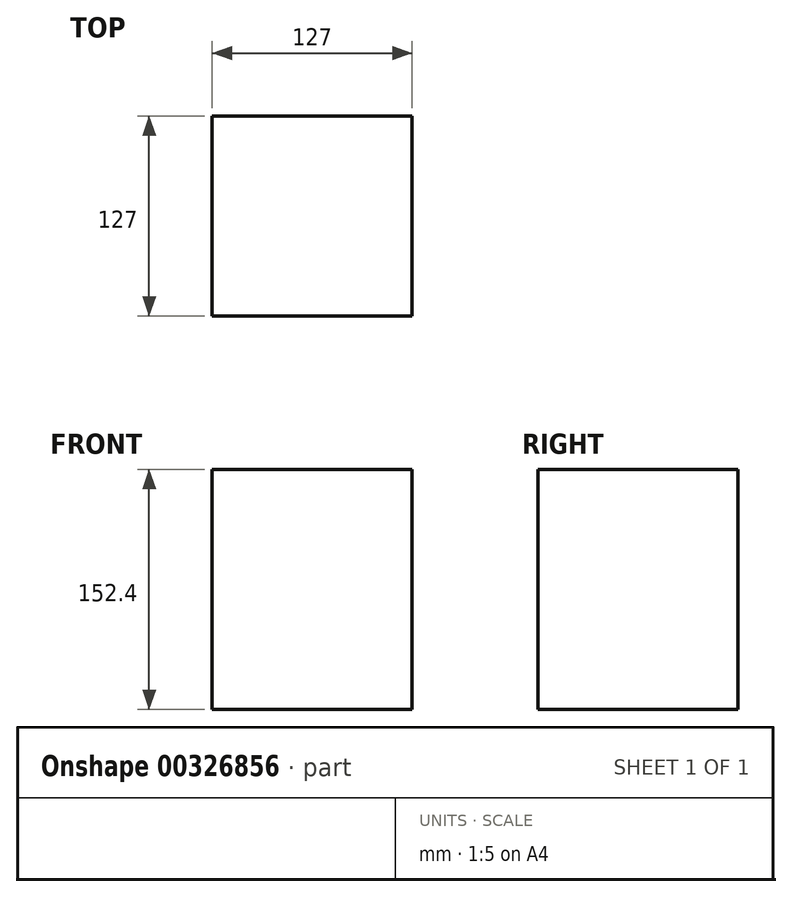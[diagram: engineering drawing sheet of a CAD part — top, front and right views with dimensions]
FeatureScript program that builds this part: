
annotation { "Feature Type Name" : "Feature", "Feature Type Description" : "" }
export const myFeature = defineFeature(function(context is Context, id is Id, definition is map)
    precondition{}
    {
        {
            var Q0;
            Q0=qCreatedBy(makeId("Top.planeOp"),FACE);
            var sketch = newSketch(context, id + "F0", { "sketchPlane" : qUnion([Q0])});
            skLineSegment(sketch, "E0.bottom", {"start": v(63.5, 63.5) * mm, "end": v(-63.5, 63.5) * mm});
            skLineSegment(sketch, "E0.top", {"start": v(63.5, -63.5) * mm, "end": v(-63.5, -63.5) * mm});
            skLineSegment(sketch, "E0.left", {"start": v(63.5, 63.5) * mm, "end": v(63.5, -63.5) * mm});
            skLineSegment(sketch, "E0.right", {"start": v(-63.5, 63.5) * mm, "end": v(-63.5, -63.5) * mm});
            skPoint(sketch, "E0.middle", {"position": v(0, 0) * mm});
            skSolve(sketch);
        }
        {
            var Q0;
            Q0 = qSketchRegion(id + "F0", true);
            extrude(context, id + "F1", {"entities" : qUnion([Q0]), "depth" : 152.4 * mm});
        }
    });
